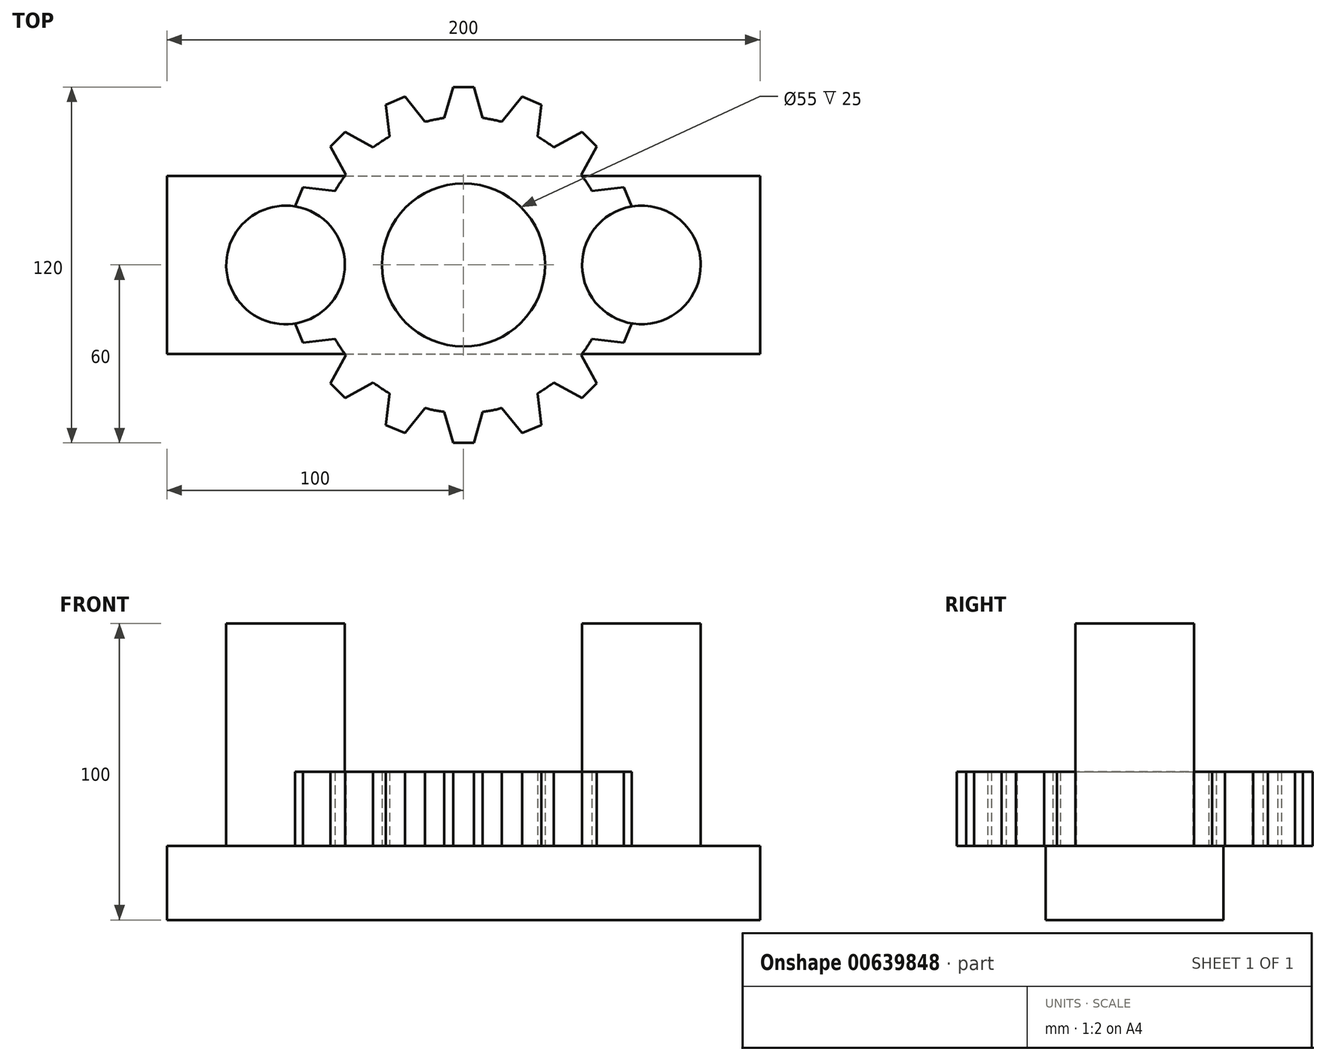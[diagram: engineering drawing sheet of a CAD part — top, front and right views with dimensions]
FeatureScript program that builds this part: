
annotation { "Feature Type Name" : "Feature", "Feature Type Description" : "" }
export const myFeature = defineFeature(function(context is Context, id is Id, definition is map)
    precondition{}
    {
        {
            var Q0;
            Q0=qCreatedBy(makeId("Top.planeOp"),FACE);
            var sketch = newSketch(context, id + "F0", { "sketchPlane" : qUnion([Q0])});
            skCircle(sketch, "E0", {"center": v(0, 0) * mm, "radius": 50 * mm});
            skLineSegment(sketch, "E1", {"start": v(0, 0) * mm, "end": v(0, 66.04) * mm, "construction": true});
            skLineSegment(sketch, "E2", {"start": v(0, 60) * mm, "end": v(-3.5, 60) * mm});
            skLineSegment(sketch, "E3", {"start": v(-3.5, 60) * mm, "end": v(-6.5, 49.58) * mm});
            skLineSegment(sketch, "E4.MirrorCS", {"start": v(0, 60) * mm, "end": v(3.5, 60) * mm});
            skLineSegment(sketch, "E5.MirrorCS", {"start": v(3.5, 60) * mm, "end": v(6.5, 49.58) * mm});
            skLineSegment(sketch, "E6.1.0", {"start": v(-22.96, 55.43) * mm, "end": v(-26.2, 54.1) * mm});
            skLineSegment(sketch, "E6.1.1", {"start": v(-26.2, 54.1) * mm, "end": v(-24.98, 43.31) * mm});
            skLineSegment(sketch, "E6.1.2", {"start": v(-22.96, 55.43) * mm, "end": v(-19.73, 56.77) * mm});
            skLineSegment(sketch, "E6.1.3", {"start": v(-19.73, 56.77) * mm, "end": v(-12.97, 48.29) * mm});
            skLineSegment(sketch, "E6.2.0", {"start": v(-42.43, 42.43) * mm, "end": v(-44.9, 39.95) * mm});
            skLineSegment(sketch, "E6.2.1", {"start": v(-44.9, 39.95) * mm, "end": v(-39.65, 30.46) * mm});
            skLineSegment(sketch, "E6.2.2", {"start": v(-42.43, 42.43) * mm, "end": v(-39.95, 44.9) * mm});
            skLineSegment(sketch, "E6.2.3", {"start": v(-39.95, 44.9) * mm, "end": v(-30.46, 39.65) * mm});
            skLineSegment(sketch, "E7.2.3.0", {"start": v(-55.43, 22.96) * mm, "end": v(-56.77, 19.73) * mm});
            skLineSegment(sketch, "E7.3.3.0", {"start": v(-56.77, 19.73) * mm, "end": v(-48.29, 12.97) * mm});
            skLineSegment(sketch, "E7.6.3.0", {"start": v(-55.43, 22.96) * mm, "end": v(-54.1, 26.2) * mm});
            skLineSegment(sketch, "E7.9.3.0", {"start": v(-54.1, 26.2) * mm, "end": v(-43.31, 24.98) * mm});
            skLineSegment(sketch, "E7.2.4.0", {"start": v(-60, 0) * mm, "end": v(-60, -3.5) * mm});
            skLineSegment(sketch, "E7.3.4.0", {"start": v(-60, -3.5) * mm, "end": v(-49.58, -6.5) * mm});
            skLineSegment(sketch, "E7.6.4.0", {"start": v(-60, 0) * mm, "end": v(-60, 3.5) * mm});
            skLineSegment(sketch, "E7.9.4.0", {"start": v(-60, 3.5) * mm, "end": v(-49.58, 6.5) * mm});
            skLineSegment(sketch, "E7.2.5.0", {"start": v(-55.43, -22.96) * mm, "end": v(-54.1, -26.2) * mm});
            skLineSegment(sketch, "E7.3.5.0", {"start": v(-54.1, -26.2) * mm, "end": v(-43.31, -24.98) * mm});
            skLineSegment(sketch, "E7.6.5.0", {"start": v(-55.43, -22.96) * mm, "end": v(-56.77, -19.73) * mm});
            skLineSegment(sketch, "E7.9.5.0", {"start": v(-56.77, -19.73) * mm, "end": v(-48.29, -12.97) * mm});
            skLineSegment(sketch, "E7.2.6.0", {"start": v(-42.43, -42.43) * mm, "end": v(-39.95, -44.9) * mm});
            skLineSegment(sketch, "E7.3.6.0", {"start": v(-39.95, -44.9) * mm, "end": v(-30.46, -39.65) * mm});
            skLineSegment(sketch, "E7.6.6.0", {"start": v(-42.43, -42.43) * mm, "end": v(-44.9, -39.95) * mm});
            skLineSegment(sketch, "E7.9.6.0", {"start": v(-44.9, -39.95) * mm, "end": v(-39.65, -30.46) * mm});
            skLineSegment(sketch, "E7.2.7.0", {"start": v(-22.96, -55.43) * mm, "end": v(-19.73, -56.77) * mm});
            skLineSegment(sketch, "E7.3.7.0", {"start": v(-19.73, -56.77) * mm, "end": v(-12.97, -48.29) * mm});
            skLineSegment(sketch, "E7.6.7.0", {"start": v(-22.96, -55.43) * mm, "end": v(-26.2, -54.1) * mm});
            skLineSegment(sketch, "E7.9.7.0", {"start": v(-26.2, -54.1) * mm, "end": v(-24.98, -43.31) * mm});
            skLineSegment(sketch, "E7.2.8.0", {"start": v(0, -60) * mm, "end": v(3.5, -60) * mm});
            skLineSegment(sketch, "E7.3.8.0", {"start": v(3.5, -60) * mm, "end": v(6.5, -49.58) * mm});
            skLineSegment(sketch, "E7.6.8.0", {"start": v(0, -60) * mm, "end": v(-3.5, -60) * mm});
            skLineSegment(sketch, "E7.9.8.0", {"start": v(-3.5, -60) * mm, "end": v(-6.5, -49.58) * mm});
            skLineSegment(sketch, "E7.2.9.0", {"start": v(22.96, -55.43) * mm, "end": v(26.2, -54.1) * mm});
            skLineSegment(sketch, "E7.3.9.0", {"start": v(26.2, -54.1) * mm, "end": v(24.98, -43.31) * mm});
            skLineSegment(sketch, "E7.6.9.0", {"start": v(22.96, -55.43) * mm, "end": v(19.73, -56.77) * mm});
            skLineSegment(sketch, "E7.9.9.0", {"start": v(19.73, -56.77) * mm, "end": v(12.97, -48.29) * mm});
            skLineSegment(sketch, "E7.2.10.0", {"start": v(42.43, -42.43) * mm, "end": v(44.9, -39.95) * mm});
            skLineSegment(sketch, "E7.3.10.0", {"start": v(44.9, -39.95) * mm, "end": v(39.65, -30.46) * mm});
            skLineSegment(sketch, "E7.6.10.0", {"start": v(42.43, -42.43) * mm, "end": v(39.95, -44.9) * mm});
            skLineSegment(sketch, "E7.9.10.0", {"start": v(39.95, -44.9) * mm, "end": v(30.46, -39.65) * mm});
            skLineSegment(sketch, "E7.2.11.0", {"start": v(55.43, -22.96) * mm, "end": v(56.77, -19.73) * mm});
            skLineSegment(sketch, "E7.3.11.0", {"start": v(56.77, -19.73) * mm, "end": v(48.29, -12.97) * mm});
            skLineSegment(sketch, "E7.6.11.0", {"start": v(55.43, -22.96) * mm, "end": v(54.1, -26.2) * mm});
            skLineSegment(sketch, "E7.9.11.0", {"start": v(54.1, -26.2) * mm, "end": v(43.31, -24.98) * mm});
            skLineSegment(sketch, "E7.2.12.0", {"start": v(60, 0) * mm, "end": v(60, 3.5) * mm});
            skLineSegment(sketch, "E7.3.12.0", {"start": v(60, 3.5) * mm, "end": v(49.58, 6.5) * mm});
            skLineSegment(sketch, "E7.6.12.0", {"start": v(60, 0) * mm, "end": v(60, -3.5) * mm});
            skLineSegment(sketch, "E7.9.12.0", {"start": v(60, -3.5) * mm, "end": v(49.58, -6.5) * mm});
            skLineSegment(sketch, "E7.2.13.0", {"start": v(55.43, 22.96) * mm, "end": v(54.1, 26.2) * mm});
            skLineSegment(sketch, "E7.3.13.0", {"start": v(54.1, 26.2) * mm, "end": v(43.31, 24.98) * mm});
            skLineSegment(sketch, "E7.6.13.0", {"start": v(55.43, 22.96) * mm, "end": v(56.77, 19.73) * mm});
            skLineSegment(sketch, "E7.9.13.0", {"start": v(56.77, 19.73) * mm, "end": v(48.29, 12.97) * mm});
            skLineSegment(sketch, "E7.2.14.0", {"start": v(42.43, 42.43) * mm, "end": v(39.95, 44.9) * mm});
            skLineSegment(sketch, "E7.3.14.0", {"start": v(39.95, 44.9) * mm, "end": v(30.46, 39.65) * mm});
            skLineSegment(sketch, "E7.6.14.0", {"start": v(42.43, 42.43) * mm, "end": v(44.9, 39.95) * mm});
            skLineSegment(sketch, "E7.9.14.0", {"start": v(44.9, 39.95) * mm, "end": v(39.65, 30.46) * mm});
            skLineSegment(sketch, "E8.2.15.0", {"start": v(22.96, 55.43) * mm, "end": v(19.73, 56.77) * mm});
            skLineSegment(sketch, "E8.3.15.0", {"start": v(19.73, 56.77) * mm, "end": v(12.97, 48.29) * mm});
            skLineSegment(sketch, "E8.6.15.0", {"start": v(22.96, 55.43) * mm, "end": v(26.2, 54.1) * mm});
            skLineSegment(sketch, "E8.9.15.0", {"start": v(26.2, 54.1) * mm, "end": v(24.98, 43.31) * mm});
            skCircle(sketch, "E9", {"center": v(0, 0) * mm, "radius": 27.5 * mm});
            skSolve(sketch);
        }
        {
            var Q0;
            Q0=makeQuery(id+"F0.imprint","IMPRINT",FACE,{"disambiguationData":[TD([[makeQuery(id+"F0.imprint","IMPRINT",EDGE,{"derivedFrom":sQuery(id+"F0.wireOp",EDGE,"E6.1.0")}),1.0]])]});
            var Q1;
            Q1=makeQuery(id+"F0.imprint","IMPRINT",FACE,{"disambiguationData":[TD([[makeQuery(id+"F0.imprint","IMPRINT",EDGE,{"derivedFrom":sQuery(id+"F0.wireOp",EDGE,"E6.2.0")}),1.0]])]});
            var Q2;
            Q2=makeQuery(id+"F0.imprint","IMPRINT",FACE,{"disambiguationData":[TD([[makeQuery(id+"F0.imprint","IMPRINT",EDGE,{"derivedFrom":sQuery(id+"F0.wireOp",EDGE,"E7.2.3.0")}),1.0]])]});
            var Q3;
            Q3=makeQuery(id+"F0.imprint","IMPRINT",FACE,{"disambiguationData":[TD([[makeQuery(id+"F0.imprint","IMPRINT",EDGE,{"derivedFrom":sQuery(id+"F0.wireOp",EDGE,"E7.2.5.0")}),1.0]])]});
            var Q4;
            Q4=makeQuery(id+"F0.imprint","IMPRINT",FACE,{"disambiguationData":[TD([[makeQuery(id+"F0.imprint","IMPRINT",EDGE,{"derivedFrom":sQuery(id+"F0.wireOp",EDGE,"E7.2.6.0")}),1.0]])]});
            var Q5;
            Q5=makeQuery(id+"F0.imprint","IMPRINT",FACE,{"disambiguationData":[TD([[makeQuery(id+"F0.imprint","IMPRINT",EDGE,{"derivedFrom":sQuery(id+"F0.wireOp",EDGE,"E7.2.7.0")}),1.0]])]});
            var Q6;
            Q6=makeQuery(id+"F0.imprint","IMPRINT",FACE,{"disambiguationData":[TD([[makeQuery(id+"F0.imprint","IMPRINT",EDGE,{"derivedFrom":sQuery(id+"F0.wireOp",EDGE,"E7.2.9.0")}),1.0]])]});
            var Q7;
            Q7=makeQuery(id+"F0.imprint","IMPRINT",FACE,{"disambiguationData":[TD([[makeQuery(id+"F0.imprint","IMPRINT",EDGE,{"derivedFrom":sQuery(id+"F0.wireOp",EDGE,"E7.2.10.0")}),1.0]])]});
            var Q8;
            Q8=makeQuery(id+"F0.imprint","IMPRINT",FACE,{"disambiguationData":[TD([[makeQuery(id+"F0.imprint","IMPRINT",EDGE,{"derivedFrom":sQuery(id+"F0.wireOp",EDGE,"E7.2.11.0")}),1.0]])]});
            var Q9;
            Q9=makeQuery(id+"F0.imprint","IMPRINT",FACE,{"disambiguationData":[TD([[makeQuery(id+"F0.imprint","IMPRINT",EDGE,{"derivedFrom":sQuery(id+"F0.wireOp",EDGE,"E7.2.12.0")}),1.0]])]});
            var Q10;
            Q10=makeQuery(id+"F0.imprint","IMPRINT",FACE,{"disambiguationData":[TD([[makeQuery(id+"F0.imprint","IMPRINT",EDGE,{"derivedFrom":sQuery(id+"F0.wireOp",EDGE,"E7.2.13.0")}),1.0]])]});
            var Q11;
            Q11=makeQuery(id+"F0.imprint","IMPRINT",FACE,{"disambiguationData":[TD([[makeQuery(id+"F0.imprint","IMPRINT",EDGE,{"derivedFrom":sQuery(id+"F0.wireOp",EDGE,"E7.2.14.0")}),1.0]])]});
            var Q12;
            Q12=makeQuery(id+"F0.imprint","IMPRINT",FACE,{"disambiguationData":[TD([[makeQuery(id+"F0.imprint","IMPRINT",EDGE,{"derivedFrom":sQuery(id+"F0.wireOp",EDGE,"E8.2.15.0")}),1.0]])]});
            var Q13;
            Q13=makeQuery(id+"F0.imprint","IMPRINT",FACE,{"disambiguationData":[TD([[makeQuery(id+"F0.imprint","IMPRINT",EDGE,{"derivedFrom":sQuery(id+"F0.wireOp",EDGE,"E2")}),1.0]])]});
            var Q14;
            Q14=makeQuery(id+"F0.imprint","IMPRINT",FACE,{"disambiguationData":[TD([[makeQuery(id+"F0.imprint","IMPRINT",EDGE,{"derivedFrom":sQuery(id+"F0.wireOp",EDGE,"E7.2.8.0")}),1.0]])]});
            var Q15;
            Q15=makeQuery(id+"F0.imprint","IMPRINT",FACE,{"disambiguationData":[TD([[makeQuery(id+"F0.imprint","IMPRINT",EDGE,{"derivedFrom":sQuery(id+"F0.wireOp",EDGE,"E7.2.4.0")}),1.0]])]});
            var Q16;
            Q16=makeQuery(id+"F0.imprint","IMPRINT",FACE,{"disambiguationData":[TD([[makeQuery(id+"F0.imprint","IMPRINT",EDGE,{"derivedFrom":sQuery(id+"F0.wireOp",EDGE,"E9")}),-1.0]])]});
            extrude(context, id + "F1", {"entities" : qUnion([Q0, Q1, Q2, Q3, Q4, Q5, Q6, Q7, Q8, Q9, Q10, Q11, Q12, Q13, Q14, Q15, Q16]), "depth" : 25 * mm, "offsetDistance" : 25 * mm});
        }
        {
            var Q0;
            Q0=qCreatedBy(makeId("Top.planeOp"),FACE);
            var sketch = newSketch(context, id + "F2", { "sketchPlane" : qUnion([Q0])});
            skLineSegment(sketch, "E10.bottom", {"start": v(-100, -30) * mm, "end": v(100, -30) * mm});
            skLineSegment(sketch, "E10.top", {"start": v(-100, 30) * mm, "end": v(100, 30) * mm});
            skLineSegment(sketch, "E10.left", {"start": v(-100, -30) * mm, "end": v(-100, 30) * mm});
            skLineSegment(sketch, "E10.right", {"start": v(100, -30) * mm, "end": v(100, 30) * mm});
            skPoint(sketch, "E10.middle", {"position": v(0, 0) * mm});
            skLineSegment(sketch, "E11", {"start": v(-100, 0) * mm, "end": v(100, 0) * mm, "construction": true});
            skCircle(sketch, "E12", {"center": v(-60, 0) * mm, "radius": 20 * mm});
            skCircle(sketch, "E13", {"center": v(60, 0) * mm, "radius": 20 * mm});
            skSolve(sketch);
        }
        {
            var Q0;
            Q0=makeQuery(id+"F2.imprint","IMPRINT",FACE,{"disambiguationData":[TD([[makeQuery(id+"F2.imprint","IMPRINT",EDGE,{"derivedFrom":sQuery(id+"F2.wireOp",EDGE,"E12")}),1.0]])]});
            var Q1;
            Q1=makeQuery(id+"F2.imprint","IMPRINT",FACE,{"disambiguationData":[TD([[makeQuery(id+"F2.imprint","IMPRINT",EDGE,{"derivedFrom":sQuery(id+"F2.wireOp",EDGE,"E10.bottom")}),1.0]])]});
            var Q2;
            Q2=makeQuery(id+"F2.imprint","IMPRINT",FACE,{"disambiguationData":[TD([[makeQuery(id+"F2.imprint","IMPRINT",EDGE,{"derivedFrom":sQuery(id+"F2.wireOp",EDGE,"E13")}),1.0]])]});
            extrude(context, id + "F3", {"entities" : qUnion([Q0, Q1, Q2]), "oppositeDirection" : true, "depth" : 25 * mm, "offsetDistance" : 25 * mm});
        }
        {
            var Q0;
            Q0=makeQuery(id+"F2.imprint","IMPRINT",FACE,{"disambiguationData":[TD([[makeQuery(id+"F2.imprint","IMPRINT",EDGE,{"derivedFrom":sQuery(id+"F2.wireOp",EDGE,"E13")}),1.0]])]});
            var Q1;
            Q1=makeQuery(id+"F2.imprint","IMPRINT",FACE,{"disambiguationData":[TD([[makeQuery(id+"F2.imprint","IMPRINT",EDGE,{"derivedFrom":sQuery(id+"F2.wireOp",EDGE,"E12")}),1.0]])]});
            extrude(context, id + "F4", {"entities" : qUnion([Q0, Q1]), "operationType" : NewBodyOperationType.ADD, "depth" : 75 * mm, "offsetDistance" : 25 * mm});
        }
    });
